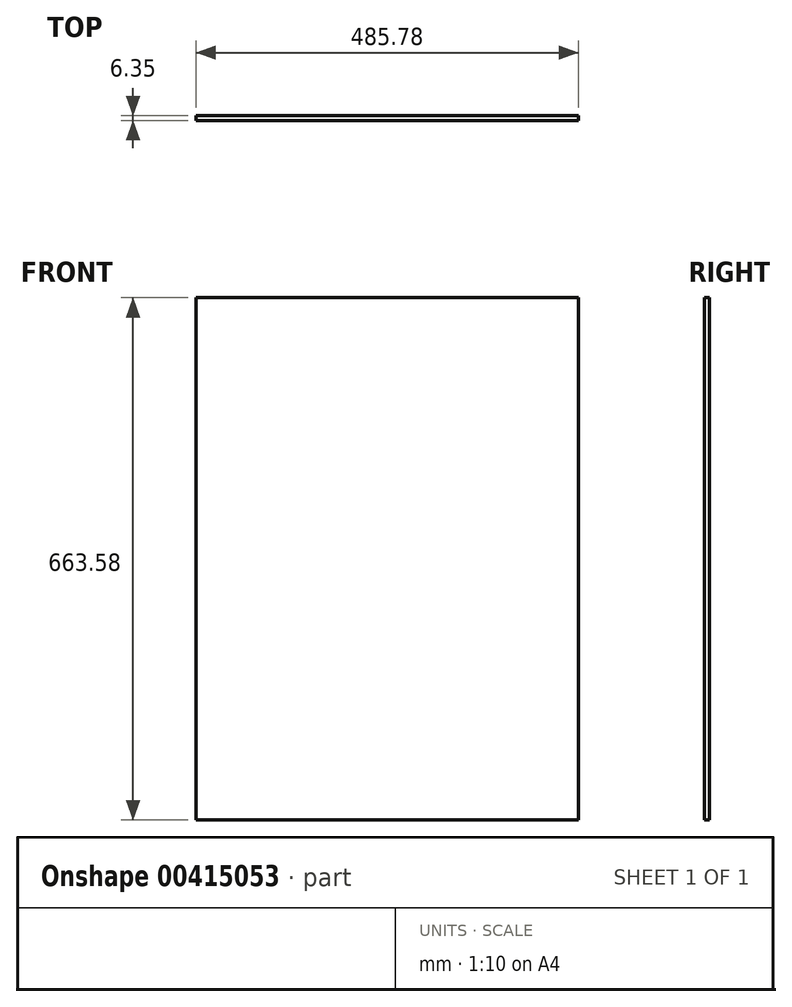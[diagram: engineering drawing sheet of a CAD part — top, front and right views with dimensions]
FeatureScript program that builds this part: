
annotation { "Feature Type Name" : "Feature", "Feature Type Description" : "" }
export const myFeature = defineFeature(function(context is Context, id is Id, definition is map)
    precondition{}
    {
        {
            var Q0;
            Q0=qCreatedBy(makeId("Front.planeOp"),FACE);
            var sketch = newSketch(context, id + "F0", { "sketchPlane" : qUnion([Q0])});
            skLineSegment(sketch, "E0.bottom", {"start": v(0, 0) * mm, "end": v(0, 0) * mm});
            skLineSegment(sketch, "E1.bottom", {"start": v(0, 0) * mm, "end": v(485.78, 0) * mm});
            skLineSegment(sketch, "E1.top", {"start": v(0, 663.58) * mm, "end": v(485.77, 663.58) * mm});
            skLineSegment(sketch, "E1.left", {"start": v(0, 0) * mm, "end": v(0, 663.58) * mm});
            skLineSegment(sketch, "E1.right", {"start": v(485.78, 0) * mm, "end": v(485.77, 663.58) * mm});
            skSolve(sketch);
        }
        {
            var Q0;
            Q0=makeQuery(id+"F0.imprint","IMPRINT",FACE,{"disambiguationData":[TD([[makeQuery(id+"F0.imprint","IMPRINT",EDGE,{"derivedFrom":sQuery(id+"F0.wireOp",EDGE,"E1.bottom")}),1.0]])]});
            extrude(context, id + "F1", {"entities" : qUnion([Q0]), "depth" : 6.35 * mm, "offsetDistance" : 25.4 * mm});
        }
    });
